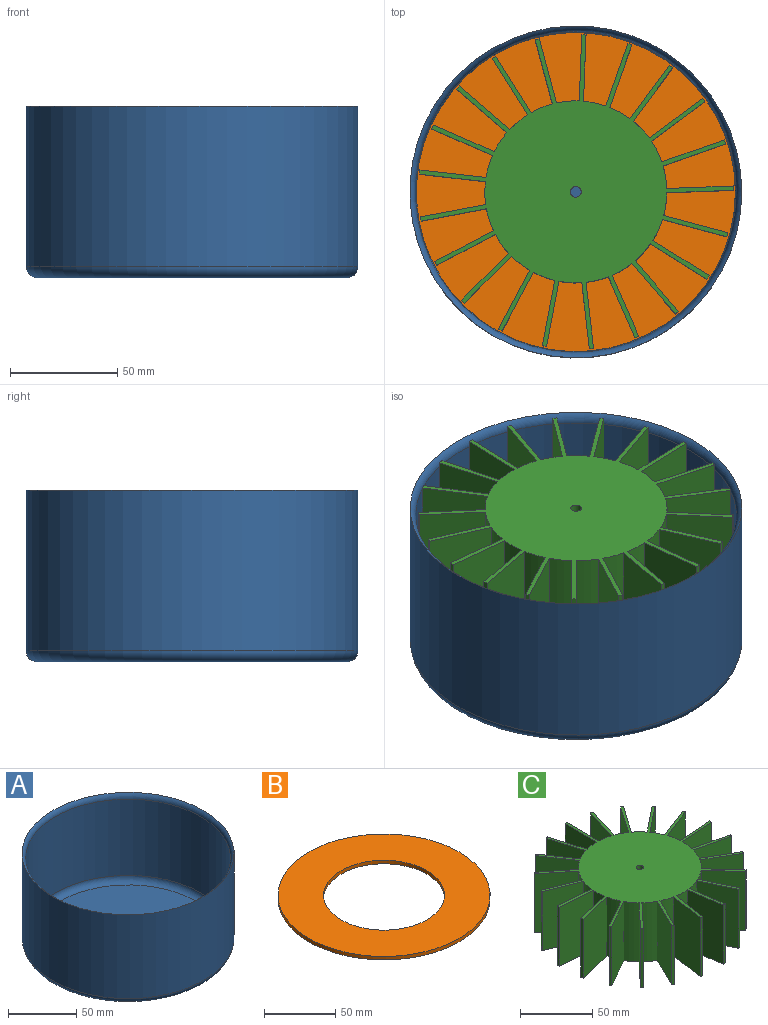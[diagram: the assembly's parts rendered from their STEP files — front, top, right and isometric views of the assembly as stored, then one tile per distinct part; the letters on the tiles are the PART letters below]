
ASSEMBLY  parts=3 mates=1
PART A: 7 faces, bbox 173.2x173.2x80.7 mm
  f0: cylinder r=77.5mm len=155mm, axis (0,0,1), area 36521mm2, adj f4,f6
  f1: plane 145x145mm, normal (0,0,-1), area 16513mm2, adj f6
  f2: cylinder r=75mm len=150mm, axis (0,0,1), area 32124.3mm2, adj f4,f5
  f3: plane 140x140mm, normal (0,0,1), area 15393.8mm2, adj f5
  f4: torus R=80mm, axis (0,0,1), area 2495.9mm2, adj f0,f2
  f5: torus R=70mm, axis (0,0,1), area 3611.4mm2, adj f2,f3
  f6: torus R=72.5mm, axis (0,0,1), area 3734.8mm2, adj f0,f1
PART B: 4 faces, bbox 149x149x3 mm
  f0: cylinder r=42.5mm len=85mm, axis (0,0,1), area 801.1mm2, adj f2,f3
  f1: cylinder r=74.5mm len=149mm, axis (0,0,1), area 1404.3mm2, adj f2,f3
  f2: plane 149x149mm, normal (0,0,-1), area 11762.1mm2, adj f0,f1
  f3: plane 149x149mm, normal (0,0,1), area 11762.1mm2, adj f0,f1
PART C: 89 faces, bbox 146.7x146.5x50 mm
  f0: plane 50x30.94mm, normal (0.07,-1,0), area 1551mm2, adj f1,f83,f84,f85
  f1: cylinder r=73.5mm len=50mm, axis (0,0,1), area 100mm2, adj f0,f2,f84,f85
  f2: plane 50x30.92mm, normal (-0.07,1,0), area 1550mm2, adj f1,f3,f84,f85
  f3: cylinder r=42.5mm len=50mm, axis (0,0,1), area 535.8mm2, adj f2,f4,f84,f85
  f4: plane 50x28.92mm, normal (0.36,-0.93,0), area 1551mm2, adj f3,f5,f84,f85
  f5: cylinder r=73.5mm len=50mm, axis (0,0,1), area 100mm2, adj f4,f6,f84,f85
  f6: plane 50x28.9mm, normal (-0.36,0.93,0), area 1550mm2, adj f5,f7,f84,f85
  f7: cylinder r=42.5mm len=50mm, axis (0,0,1), area 535.8mm2, adj f6,f8,f84,f85
  f8: plane 50x24.33mm, normal (0.62,-0.78,0), area 1551mm2, adj f7,f9,f84,f85
  f9: cylinder r=73.5mm len=50mm, axis (0,0,1), area 100mm2, adj f8,f10,f84,f85
  f10: plane 50x24.31mm, normal (-0.62,0.78,0), area 1550mm2, adj f9,f11,f84,f85
  f11: cylinder r=42.5mm len=50mm, axis (0,0,1), area 535.8mm2, adj f10,f12,f84,f85
  f12: plane 50x25.56mm, normal (0.82,-0.57,0), area 1551mm2, adj f11,f13,f84,f85
  f13: cylinder r=73.5mm len=50mm, axis (0,0,1), area 100mm2, adj f12,f14,f84,f85
  f14: plane 50x25.54mm, normal (-0.82,0.57,0), area 1550mm2, adj f13,f15,f84,f85
  f15: cylinder r=42.5mm len=50mm, axis (0,0,1), area 535.8mm2, adj f14,f16,f84,f85
  f16: plane 50x29.61mm, normal (0.95,-0.3,0), area 1551mm2, adj f15,f17,f84,f85
  f17: cylinder r=73.5mm len=50mm, axis (0,0,1), area 100mm2, adj f16,f18,f84,f85
  f18: plane 50x29.59mm, normal (-0.95,0.3,0), area 1550mm2, adj f17,f19,f84,f85
  f19: cylinder r=42.5mm len=50mm, axis (0,0,1), area 535.8mm2, adj f18,f20,f84,f85
  f20: plane 50x31.02mm, normal (1,0,0), area 1551mm2, adj f19,f21,f84,f85
  f21: cylinder r=73.5mm len=50mm, axis (0,0,1), area 100mm2, adj f20,f22,f84,f85
  f22: plane 50x31mm, normal (-1,0,0), area 1550mm2, adj f21,f23,f84,f85
  f23: cylinder r=42.5mm len=50mm, axis (0,0,1), area 535.8mm2, adj f22,f24,f84,f85
  f24: plane 50x29.68mm, normal (0.96,0.29,0), area 1551mm2, adj f23,f25,f84,f85
  f25: cylinder r=73.5mm len=50mm, axis (0,0,1), area 100mm2, adj f24,f26,f84,f85
  f26: plane 50x29.66mm, normal (-0.96,-0.29,0), area 1550mm2, adj f25,f27,f84,f85
  f27: cylinder r=42.5mm len=50mm, axis (0,0,1), area 535.8mm2, adj f26,f28,f84,f85
  f28: plane 50x25.7mm, normal (0.83,0.56,0), area 1551mm2, adj f27,f29,f84,f85
  f29: cylinder r=73.5mm len=50mm, axis (0,0,1), area 100mm2, adj f28,f30,f84,f85
  f30: plane 50x25.68mm, normal (-0.83,-0.56,0), area 1550mm2, adj f29,f31,f84,f85
  f31: cylinder r=42.5mm len=50mm, axis (0,0,1), area 535.8mm2, adj f30,f32,f84,f85
  f32: plane 50x24.18mm, normal (0.63,0.78,0), area 1551mm2, adj f31,f33,f84,f85
  f33: cylinder r=73.5mm len=50mm, axis (0,0,1), area 100mm2, adj f32,f34,f84,f85
  f34: plane 50x24.16mm, normal (-0.63,-0.78,0), area 1550mm2, adj f33,f35,f84,f85
  f35: cylinder r=42.5mm len=50mm, axis (0,0,1), area 535.8mm2, adj f34,f36,f84,f85
  f36: plane 50x28.83mm, normal (0.37,0.93,0), area 1551mm2, adj f35,f37,f84,f85
  f37: cylinder r=73.5mm len=50mm, axis (0,0,1), area 100mm2, adj f36,f38,f84,f85
  f38: plane 50x28.81mm, normal (-0.37,-0.93,0), area 1550mm2, adj f37,f39,f84,f85
  f39: cylinder r=42.5mm len=50mm, axis (0,0,1), area 535.8mm2, adj f38,f40,f84,f85
  f40: plane 50x30.92mm, normal (0.08,1,0), area 1551mm2, adj f39,f41,f84,f85
  f41: cylinder r=73.5mm len=50mm, axis (0,0,1), area 100mm2, adj f40,f42,f84,f85
  f42: plane 50x30.9mm, normal (-0.08,-1,0), area 1550mm2, adj f41,f43,f84,f85
  f43: cylinder r=42.5mm len=50mm, axis (0,0,1), area 535.8mm2, adj f42,f44,f84,f85
  f44: plane 50x30.27mm, normal (-0.22,0.98,0), area 1551mm2, adj f43,f45,f84,f85
  f45: cylinder r=73.5mm len=50mm, axis (0,0,1), area 100mm2, adj f44,f46,f84,f85
  f46: plane 50x30.25mm, normal (0.22,-0.98,0), area 1550mm2, adj f45,f47,f84,f85
  f47: cylinder r=42.5mm len=50mm, axis (0,0,1), area 535.8mm2, adj f46,f48,f84,f85
  f48: plane 50x26.93mm, normal (-0.5,0.87,0), area 1551mm2, adj f47,f49,f84,f85
  f49: cylinder r=73.5mm len=50mm, axis (0,0,1), area 100mm2, adj f48,f50,f84,f85
  f50: plane 50x26.91mm, normal (0.5,-0.87,0), area 1550mm2, adj f49,f51,f84,f85
  f51: cylinder r=42.5mm len=50mm, axis (0,0,1), area 535.8mm2, adj f50,f52,f84,f85
  f52: plane 50x22.66mm, normal (-0.73,0.68,0), area 1551mm2, adj f51,f53,f84,f85
  f53: cylinder r=73.5mm len=50mm, axis (0,0,1), area 100mm2, adj f52,f54,f84,f85
  f54: plane 50x22.64mm, normal (0.73,-0.68,0), area 1550mm2, adj f53,f55,f84,f85
  f55: cylinder r=42.5mm len=50mm, axis (0,0,1), area 535.8mm2, adj f54,f56,f84,f85
  f56: plane 50x27.89mm, normal (-0.9,0.44,0), area 1551mm2, adj f55,f57,f84,f85
  f57: cylinder r=73.5mm len=50mm, axis (0,0,1), area 100mm2, adj f56,f58,f84,f85
  f58: plane 50x27.88mm, normal (0.9,-0.44,0), area 1550mm2, adj f57,f59,f84,f85
  f59: cylinder r=42.5mm len=50mm, axis (0,0,1), area 535.8mm2, adj f58,f60,f84,f85
  f60: plane 50x30.66mm, normal (-0.99,0.15,0), area 1551mm2, adj f59,f61,f84,f85
  f61: cylinder r=73.5mm len=50mm, axis (0,0,1), area 100mm2, adj f60,f62,f84,f85
  f62: plane 50x30.64mm, normal (0.99,-0.15,0), area 1550mm2, adj f61,f63,f84,f85
  f63: cylinder r=42.5mm len=50mm, axis (0,0,1), area 535.8mm2, adj f62,f64,f84,f85
  f64: plane 50x30.69mm, normal (-0.99,-0.15,0), area 1551mm2, adj f63,f65,f84,f85
  f65: cylinder r=73.5mm len=50mm, axis (0,0,1), area 100mm2, adj f64,f66,f84,f85
  f66: plane 50x30.67mm, normal (0.99,0.15,0), area 1550mm2, adj f65,f67,f84,f85
  f67: cylinder r=42.5mm len=50mm, axis (0,0,1), area 535.8mm2, adj f66,f68,f84,f85
  f68: plane 50x28mm, normal (-0.9,-0.43,0), area 1551mm2, adj f67,f69,f84,f85
  f69: cylinder r=73.5mm len=50mm, axis (0,0,1), area 100mm2, adj f68,f70,f84,f85
  f70: plane 50x27.98mm, normal (0.9,0.43,0), area 1550mm2, adj f69,f71,f84,f85
  f71: cylinder r=42.5mm len=50mm, axis (0,0,1), area 535.3mm2, adj f70,f72,f84,f85
  f72: plane 50x22.83mm, normal (-0.74,-0.68,0), area 1551mm2, adj f71,f73,f84,f85
  f73: cylinder r=73.5mm len=50mm, axis (0,0,1), area 100mm2, adj f72,f74,f84,f85
  f74: plane 50x22.81mm, normal (0.74,0.68,0), area 1550mm2, adj f73,f75,f84,f85
  f75: cylinder r=42.5mm len=50mm, axis (0,0,1), area 536.2mm2, adj f74,f76,f84,f85
  f76: plane 50x26.8mm, normal (-0.5,-0.86,0), area 1551mm2, adj f75,f77,f84,f85
  f77: cylinder r=73.5mm len=50mm, axis (0,0,1), area 100mm2, adj f76,f78,f84,f85
  f78: plane 50x26.79mm, normal (0.5,0.86,0), area 1550mm2, adj f77,f79,f84,f85
  f79: cylinder r=42.5mm len=50mm, axis (0,0,1), area 536.8mm2, adj f78,f80,f84,f85
  f80: plane 50x30.22mm, normal (-0.23,-0.97,0), area 1551mm2, adj f79,f81,f84,f85
  f81: cylinder r=73.5mm len=50mm, axis (0,0,1), area 100mm2, adj f80,f82,f84,f85
  f82: plane 50x30.2mm, normal (0.23,0.97,0), area 1550mm2, adj f81,f83,f84,f85
  f83: cylinder r=42.5mm len=50mm, axis (0,0,1), area 534.7mm2, adj f0,f82,f84,f85
  f84: plane 146.7x146.48mm, normal (0,0,-1), area 3658.5mm2, adj f0,f1,f2,f3,f4,f5,f6,f7
  f85: plane 146.7x146.48mm, normal (0,0,1), area 6957.1mm2, adj f0,f1,f2,f3,f4,f5,f6,f7
  f86: cylinder r=32.5mm len=65mm, axis (0,0,-1), area 5105.1mm2, adj f84,f87
  f87: plane 65x65mm, normal (0,0,-1), area 3298.7mm2, adj f86,f88
  f88: cylinder r=2.5mm len=25mm, axis (0,0,1), area 392.7mm2, adj f85,f87
PLACE A t=(2.82,-14.2,-3.74)mm fixed
PLACE B t=(2.82,-14.2,-53.74)mm
PLACE C rot(axis=(0,0,-1),70.5deg) t=(2.82,-14.2,-3.74)mm
MATE revolute C.f86 <-> B.f0  axis (0,0,-1) through (2.82,-14.2,-53.74)mm
